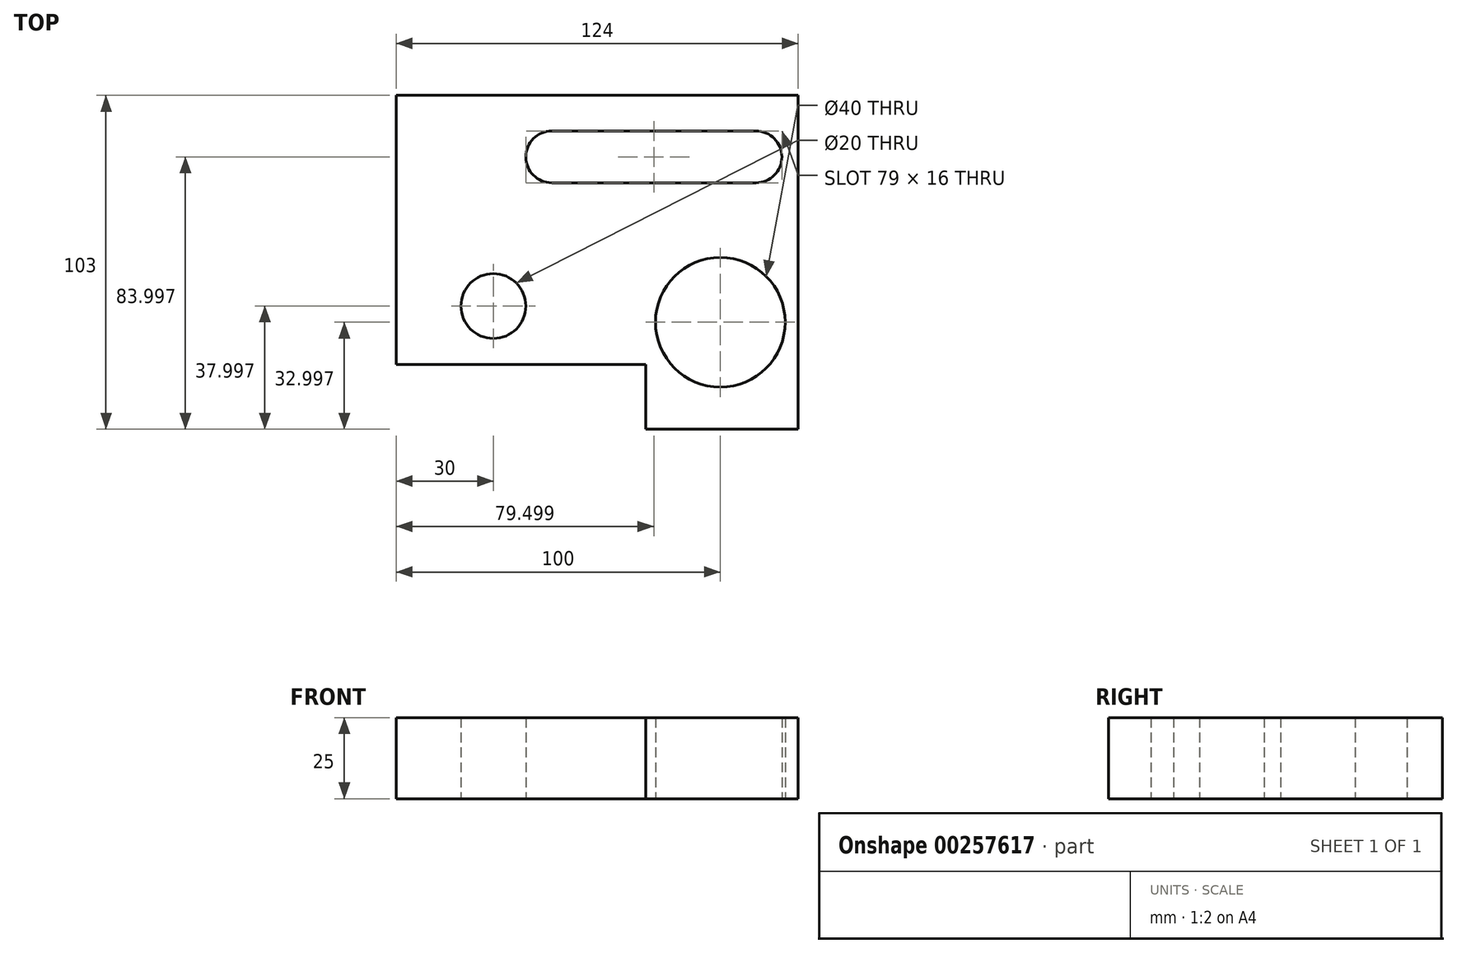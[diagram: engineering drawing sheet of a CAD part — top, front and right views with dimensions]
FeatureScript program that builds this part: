
annotation { "Feature Type Name" : "Feature", "Feature Type Description" : "" }
export const myFeature = defineFeature(function(context is Context, id is Id, definition is map)
    precondition{}
    {
        {
            var Q0;
            Q0=qCreatedBy(makeId("Top.planeOp"),FACE);
            var sketch = newSketch(context, id + "F0", { "sketchPlane" : qUnion([Q0])});
            skLineSegment(sketch, "E0", {"start": v(-51.42, 39.17) * mm, "end": v(-51.42, -43.83) * mm});
            skLineSegment(sketch, "E1", {"start": v(-51.42, 39.17) * mm, "end": v(72.58, 39.17) * mm});
            skLineSegment(sketch, "E2", {"start": v(72.58, 39.17) * mm, "end": v(72.58, -63.83) * mm});
            skLineSegment(sketch, "E3", {"start": v(72.58, -63.83) * mm, "end": v(25.58, -63.83) * mm});
            skLineSegment(sketch, "E4", {"start": v(25.58, -63.83) * mm, "end": v(25.58, -43.83) * mm});
            skLineSegment(sketch, "E5", {"start": v(25.58, -43.83) * mm, "end": v(-51.42, -43.83) * mm});
            skLineSegment(sketch, "E6", {"start": v(72.58, -63.83) * mm, "end": v(49.08, -63.83) * mm});
            skLineSegment(sketch, "E7", {"start": v(-51.42, -43.83) * mm, "end": v(25.58, -43.83) * mm});
            skCircle(sketch, "E8", {"center": v(48.58, -30.83) * mm, "radius": 20 * mm});
            skLineSegment(sketch, "E9", {"start": v(-51.42, -43.83) * mm, "end": v(-21.42, -43.83) * mm});
            skLineSegment(sketch, "E10", {"start": v(-51.42, 39.17) * mm, "end": v(-51.42, -25.83) * mm});
            skCircle(sketch, "E11", {"center": v(-21.42, -25.83) * mm, "radius": 10 * mm});
            skPoint(sketch, "E12.trimOffspring.end.orphan", {"position": v(48.58, -43.83) * mm});
            skLineSegment(sketch, "E13", {"start": v(72.58, 39.17) * mm, "end": v(72.58, 25.17) * mm});
            skLineSegment(sketch, "E14", {"start": v(59.58, 28.17) * mm, "end": v(-3.42, 28.17) * mm});
            skLineSegment(sketch, "E15", {"start": v(-11.42, 20.17) * mm, "end": v(-11.42, 20.17) * mm});
            skLineSegment(sketch, "E16", {"start": v(-3.42, 12.17) * mm, "end": v(59.58, 12.17) * mm});
            skLineSegment(sketch, "E17", {"start": v(67.58, 20.17) * mm, "end": v(67.58, 20.17) * mm});
            skPoint(sketch, "E18.visualSharp", {"position": v(-11.42, 28.17) * mm});
            skArc(sketch, "E18.filletArc", {"start": v(-3.42, 28.17) * mm, "mid": v(-9.08, 25.82) * mm, "end": v(-11.42, 20.17) * mm});
            skPoint(sketch, "E19.visualSharp", {"position": v(-11.42, 12.17) * mm});
            skArc(sketch, "E19.filletArc", {"start": v(-11.42, 20.17) * mm, "mid": v(-9.08, 14.5) * mm, "end": v(-3.42, 12.17) * mm});
            skPoint(sketch, "E20.visualSharp", {"position": v(67.58, 28.17) * mm});
            skArc(sketch, "E20.filletArc", {"start": v(67.58, 20.17) * mm, "mid": v(65.24, 25.82) * mm, "end": v(59.58, 28.17) * mm});
            skPoint(sketch, "E21.visualSharp", {"position": v(67.58, 12.17) * mm});
            skArc(sketch, "E21.filletArc", {"start": v(59.58, 12.17) * mm, "mid": v(65.24, 14.5) * mm, "end": v(67.58, 20.17) * mm});
            skSolve(sketch);
        }
        {
            var Q0;
            Q0=makeQuery(id+"F0.imprint","IMPRINT",FACE,{"disambiguationData":[TD([[makeQuery(id+"F0.imprint","IMPRINT",EDGE,{"derivedFrom":sQuery(id+"F0.wireOp",EDGE,"E0")}),1.0]])]});
            extrude(context, id + "F1", {"entities" : qUnion([Q0]), "depth" : 25 * mm});
        }
    });
